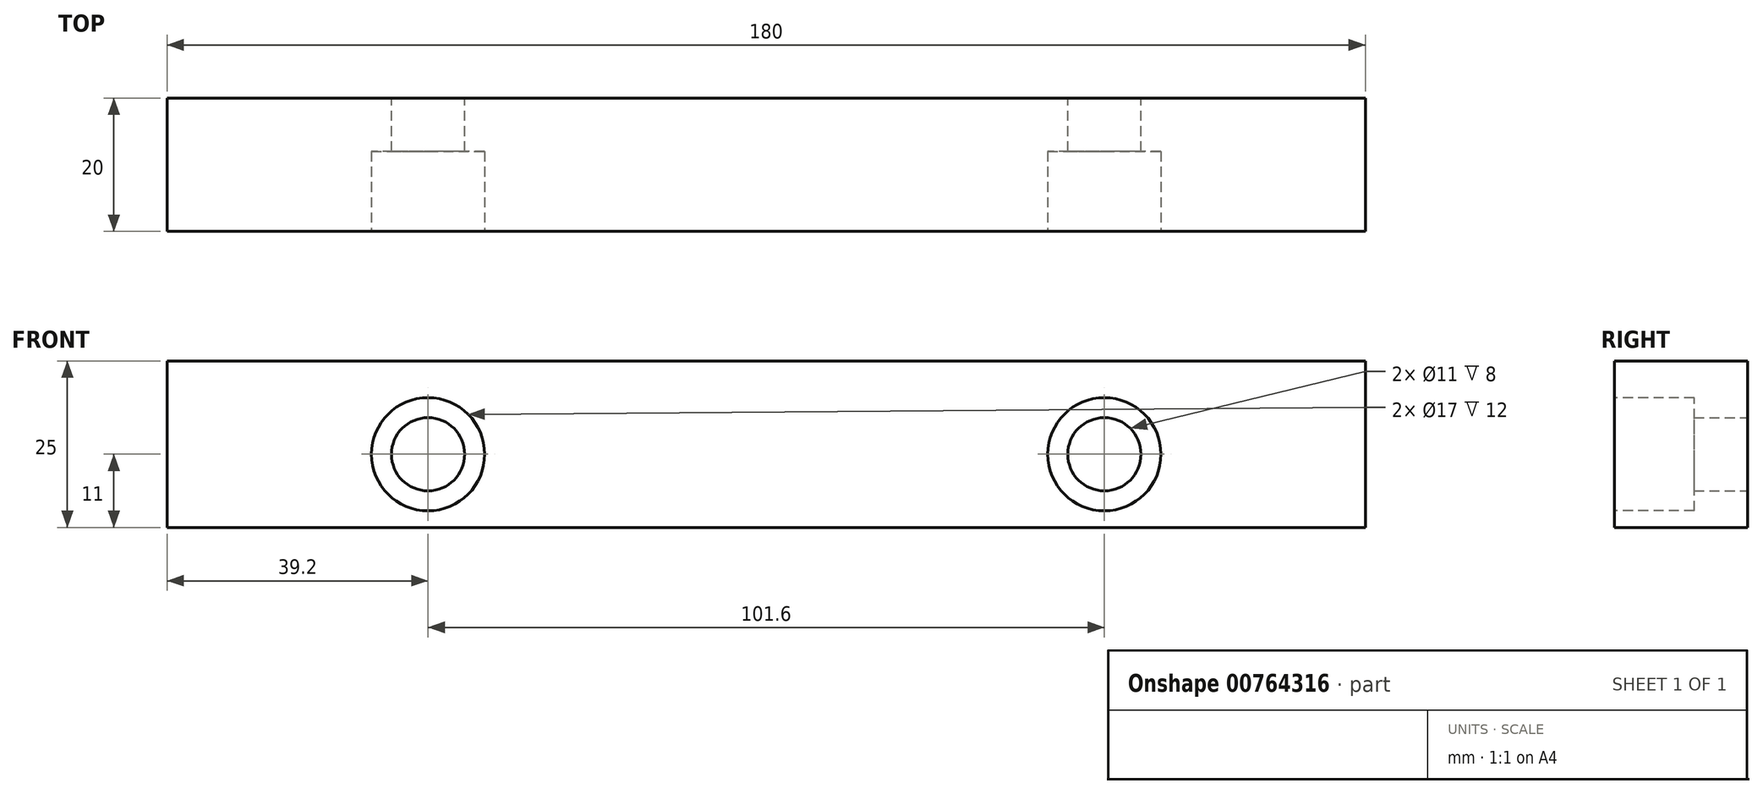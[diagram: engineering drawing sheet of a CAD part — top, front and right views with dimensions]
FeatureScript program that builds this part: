
annotation { "Feature Type Name" : "Feature", "Feature Type Description" : "" }
export const myFeature = defineFeature(function(context is Context, id is Id, definition is map)
    precondition{}
    {
        {
            var Q0;
            Q0=qCreatedBy(makeId("Front.planeOp"),FACE);
            var sketch = newSketch(context, id + "F0", { "sketchPlane" : qUnion([Q0])});
            skLineSegment(sketch, "E0.bottom", {"start": v(0, 0) * mm, "end": v(180, 0) * mm});
            skLineSegment(sketch, "E0.top", {"start": v(0, 25) * mm, "end": v(180, 25) * mm});
            skLineSegment(sketch, "E0.left", {"start": v(0, 0) * mm, "end": v(0, 25) * mm});
            skLineSegment(sketch, "E0.right", {"start": v(180, 0) * mm, "end": v(180, 25) * mm});
            skCircle(sketch, "E1", {"center": v(39.2, 11) * mm, "radius": 5.5 * mm});
            skCircle(sketch, "E2", {"center": v(140.8, 11) * mm, "radius": 5.5 * mm});
            skLineSegment(sketch, "E3", {"start": v(39.2, 11) * mm, "end": v(0, 11) * mm, "construction": true});
            skLineSegment(sketch, "E4", {"start": v(140.8, 11) * mm, "end": v(180, 11) * mm, "construction": true});
            skSolve(sketch);
        }
        {
            var Q0;
            Q0=makeQuery(id+"F0.imprint","IMPRINT",FACE,{"disambiguationData":[TD([[makeQuery(id+"F0.imprint","IMPRINT",EDGE,{"derivedFrom":sQuery(id+"F0.wireOp",EDGE,"E0.bottom")}),1.0]])]});
            extrude(context, id + "F1", {"entities" : qUnion([Q0]), "depth" : 20 * mm, "offsetDistance" : 25 * mm});
        }
        {
            var Q0;
            Q0=makeQuery(id+"F1.opExtrude","CAP_FACE",FACE,{"disambiguationData":[OSD([sQuery(id+"F0.wireOp",EDGE,"E0.bottom"),sQuery(id+"F0.wireOp",EDGE,"E0.top"),sQuery(id+"F0.wireOp",EDGE,"E0.left"),sQuery(id+"F0.wireOp",EDGE,"E0.right"),sQuery(id+"F0.wireOp",EDGE,"E1"),sQuery(id+"F0.wireOp",EDGE,"E2")])],"isStart":false});
            var sketch = newSketch(context, id + "F2", { "sketchPlane" : qUnion([Q0])});
            skCircle(sketch, "E5", {"center": v(39.2, 11) * mm, "radius": 8.5 * mm});
            skCircle(sketch, "E6", {"center": v(140.8, 11) * mm, "radius": 8.5 * mm});
            skSolve(sketch);
        }
        {
            var Q0;
            Q0=makeQuery(id+"F2.imprint","IMPRINT",FACE,{"disambiguationData":[TD([[makeQuery(id+"F2.imprint","IMPRINT",EDGE,{"derivedFrom":sQuery(id+"F2.wireOp",EDGE,"E5")}),1.0]])]});
            var Q1;
            Q1=makeQuery(id+"F2.imprint","IMPRINT",FACE,{"disambiguationData":[TD([[makeQuery(id+"F2.imprint","IMPRINT",EDGE,{"derivedFrom":sQuery(id+"F2.wireOp",EDGE,"E6")}),1.0]])]});
            extrude(context, id + "F3", {"entities" : qUnion([Q0, Q1]), "operationType" : NewBodyOperationType.REMOVE, "oppositeDirection" : true, "depth" : 12 * mm, "offsetDistance" : 25 * mm});
        }
    });
